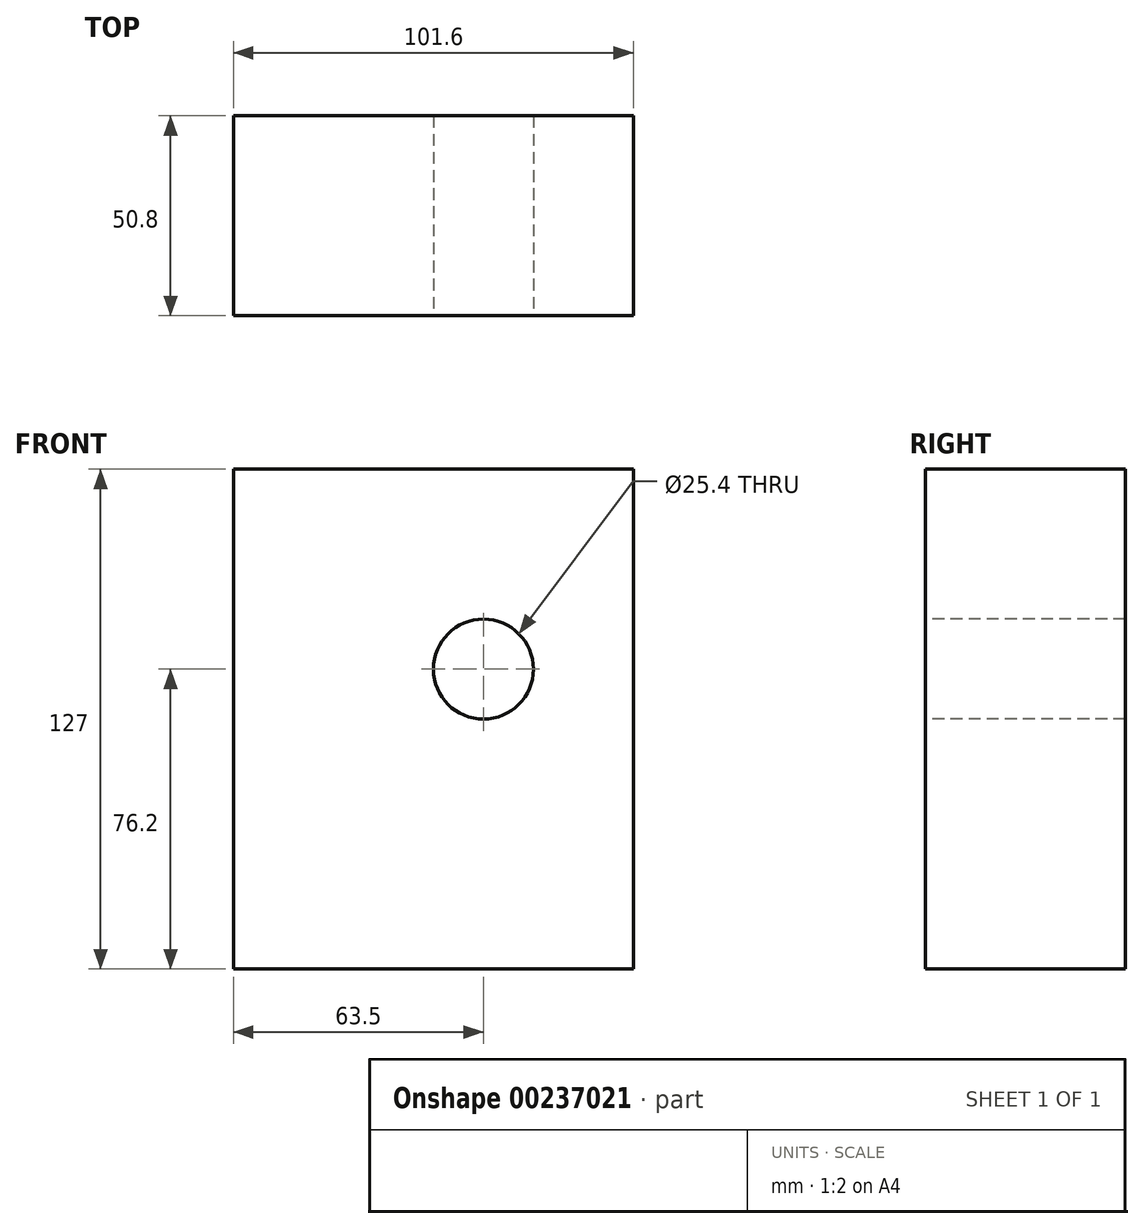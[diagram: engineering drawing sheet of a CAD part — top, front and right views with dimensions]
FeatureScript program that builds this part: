
annotation { "Feature Type Name" : "Feature", "Feature Type Description" : "" }
export const myFeature = defineFeature(function(context is Context, id is Id, definition is map)
    precondition{}
    {
        {
            var Q0;
            Q0=qCreatedBy(makeId("Front.planeOp"),FACE);
            var sketch = newSketch(context, id + "F0", { "sketchPlane" : qUnion([Q0])});
            skLineSegment(sketch, "E0.bottom", {"start": v(50.8, -63.5) * mm, "end": v(-50.8, -63.5) * mm});
            skLineSegment(sketch, "E0.top", {"start": v(50.8, 63.5) * mm, "end": v(-50.8, 63.5) * mm});
            skLineSegment(sketch, "E0.left", {"start": v(50.8, -63.5) * mm, "end": v(50.8, 63.5) * mm});
            skLineSegment(sketch, "E0.right", {"start": v(-50.8, -63.5) * mm, "end": v(-50.8, 63.5) * mm});
            skPoint(sketch, "E0.middle", {"position": v(0, 0) * mm});
            skSolve(sketch);
        }
        {
            var Q0;
            Q0=makeQuery(id+"F0.imprint","IMPRINT",FACE,{"disambiguationData":[TD([[makeQuery(id+"F0.imprint","IMPRINT",EDGE,{"derivedFrom":sQuery(id+"F0.wireOp",EDGE,"E0.bottom")}),-1.0]])]});
            var sketch = newSketch(context, id + "F1", { "sketchPlane" : qUnion([Q0])});
            skCircle(sketch, "E1", {"center": v(12.7, 12.7) * mm, "radius": 12.7 * mm});
            skSolve(sketch);
        }
        {
            var Q0;
            Q0=makeQuery(id+"F0.imprint","IMPRINT",FACE,{"disambiguationData":[TD([[makeQuery(id+"F0.imprint","IMPRINT",EDGE,{"derivedFrom":sQuery(id+"F0.wireOp",EDGE,"E0.bottom")}),-1.0]])]});
            extrude(context, id + "F2", {"entities" : qUnion([Q0]), "oppositeDirection" : true, "depth" : 50.8 * mm});
        }
        {
            var Q0;
            Q0=makeQuery(id+"F1.imprint","IMPRINT",FACE,{"disambiguationData":[TD([[makeQuery(id+"F1.imprint","IMPRINT",EDGE,{"derivedFrom":sQuery(id+"F1.wireOp",EDGE,"E1")}),1.0]])]});
            extrude(context, id + "F3", {"entities" : qUnion([Q0]), "operationType" : NewBodyOperationType.REMOVE, "endBound" : BoundingType.THROUGH_ALL, "oppositeDirection" : true, "depth" : 25.4 * mm});
        }
    });
